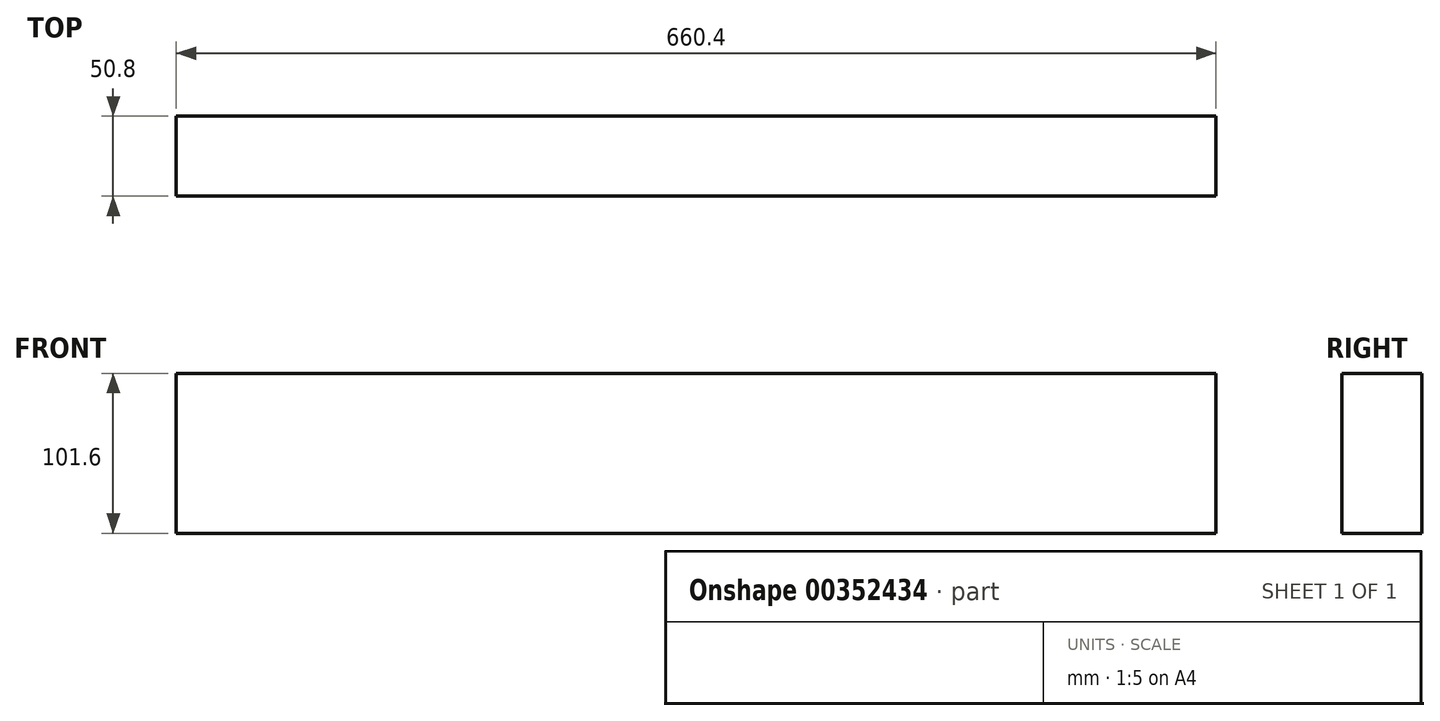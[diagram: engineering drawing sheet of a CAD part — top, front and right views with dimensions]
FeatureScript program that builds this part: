
annotation { "Feature Type Name" : "Feature", "Feature Type Description" : "" }
export const myFeature = defineFeature(function(context is Context, id is Id, definition is map)
    precondition{}
    {
        {
            var Q0;
            Q0=qCreatedBy(makeId("Right.planeOp"),FACE);
            var sketch = newSketch(context, id + "F0", { "sketchPlane" : qUnion([Q0])});
            skLineSegment(sketch, "E0.bottom", {"start": v(0, 0) * mm, "end": v(50.8, 0) * mm});
            skLineSegment(sketch, "E0.top", {"start": v(0, 101.6) * mm, "end": v(50.8, 101.6) * mm});
            skLineSegment(sketch, "E0.left", {"start": v(0, 0) * mm, "end": v(0, 101.6) * mm});
            skLineSegment(sketch, "E0.right", {"start": v(50.8, 0) * mm, "end": v(50.8, 101.6) * mm});
            skSolve(sketch);
        }
        {
            var Q0;
            Q0=makeQuery(id+"F0.imprint","IMPRINT",FACE,{"disambiguationData":[TD([[makeQuery(id+"F0.imprint","IMPRINT",EDGE,{"derivedFrom":sQuery(id+"F0.wireOp",EDGE,"E0.bottom")}),1.0]])]});
            extrude(context, id + "F1", {"entities" : qUnion([Q0]), "depth" : 660.4 * mm});
        }
    });
